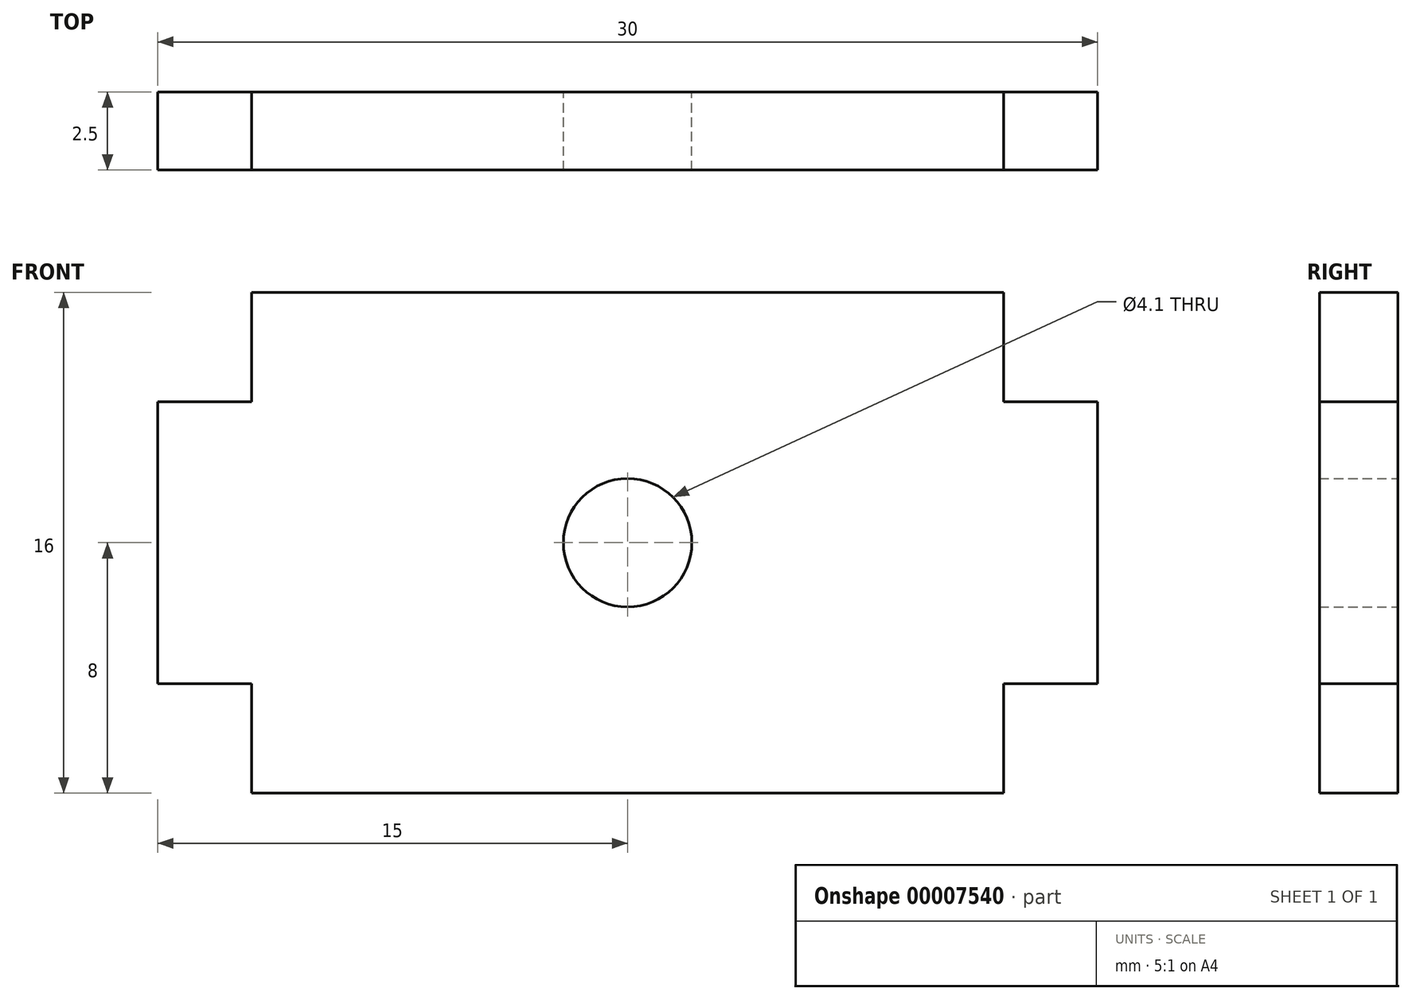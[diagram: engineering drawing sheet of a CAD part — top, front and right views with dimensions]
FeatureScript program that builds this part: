
annotation { "Feature Type Name" : "Feature", "Feature Type Description" : "" }
export const myFeature = defineFeature(function(context is Context, id is Id, definition is map)
    precondition{}
    {
        {
            var Q0;
            Q0=qCreatedBy(makeId("Front.planeOp"),FACE);
            var sketch = newSketch(context, id + "F0", { "sketchPlane" : qUnion([Q0])});
            skLineSegment(sketch, "E0.rect.bottom", {"start": v(12, -8) * mm, "end": v(-12, -8) * mm});
            skLineSegment(sketch, "E0.rect.top", {"start": v(12, 8) * mm, "end": v(-12, 8) * mm});
            skLineSegment(sketch, "E0.rect.left", {"start": v(12, -8) * mm, "end": v(12, -4.5) * mm});
            skLineSegment(sketch, "E0.rect.right", {"start": v(-12, -8) * mm, "end": v(-12, -4.5) * mm});
            skPoint(sketch, "E0.rect.middle", {"position": v(0, 0) * mm});
            skLineSegment(sketch, "E1.rect.bottom", {"start": v(15, -4.5) * mm, "end": v(12, -4.5) * mm});
            skLineSegment(sketch, "E1.rect.top", {"start": v(15, 4.5) * mm, "end": v(12, 4.5) * mm});
            skLineSegment(sketch, "E1.rect.left", {"start": v(15, -4.5) * mm, "end": v(15, 4.5) * mm});
            skLineSegment(sketch, "E1.rect.right", {"start": v(-15, -4.5) * mm, "end": v(-15, 4.5) * mm});
            skLineSegment(sketch, "E2.trimOffspring", {"start": v(-12, 4.5) * mm, "end": v(-15, 4.5) * mm});
            skLineSegment(sketch, "E3.trimOffspring", {"start": v(-12, 4.5) * mm, "end": v(-12, 8) * mm});
            skLineSegment(sketch, "E4.trimOffspring", {"start": v(-12, -4.5) * mm, "end": v(-15, -4.5) * mm});
            skLineSegment(sketch, "E5.trimOffspring", {"start": v(12, 4.5) * mm, "end": v(12, 8) * mm});
            skCircle(sketch, "E6", {"center": v(0, 0) * mm, "radius": 2.05 * mm});
            skSolve(sketch);
        }
        {
            var Q0;
            Q0 = qSketchRegion(id + "F0", true);
            extrude(context, id + "F1", {"entities" : qUnion([Q0]), "depth" : 2.5 * mm});
        }
    });
